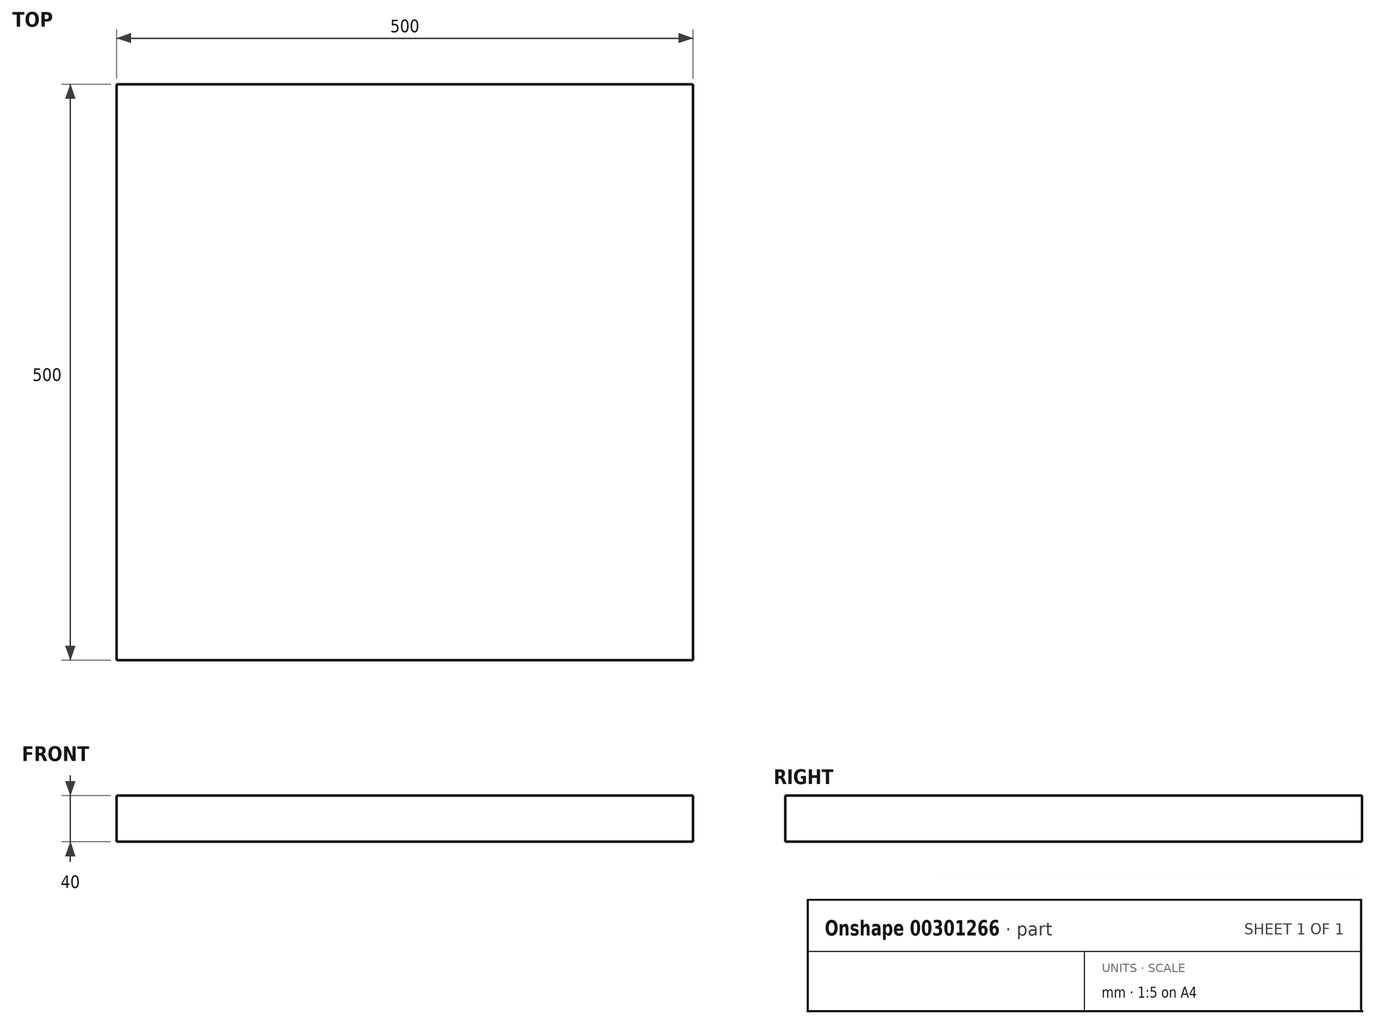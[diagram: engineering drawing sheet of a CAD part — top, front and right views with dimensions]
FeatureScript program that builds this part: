
annotation { "Feature Type Name" : "Feature", "Feature Type Description" : "" }
export const myFeature = defineFeature(function(context is Context, id is Id, definition is map)
    precondition{}
    {
        {
            var Q0;
            Q0=qCreatedBy(makeId("Top.planeOp"),FACE);
            var sketch = newSketch(context, id + "F0", { "sketchPlane" : qUnion([Q0])});
            skLineSegment(sketch, "E0.bottom", {"start": v(-250, 250) * mm, "end": v(250, 250) * mm});
            skLineSegment(sketch, "E0.top", {"start": v(-250, -250) * mm, "end": v(250, -250) * mm});
            skLineSegment(sketch, "E0.left", {"start": v(-250, 250) * mm, "end": v(-250, -250) * mm});
            skLineSegment(sketch, "E0.right", {"start": v(250, 250) * mm, "end": v(250, -250) * mm});
            skPoint(sketch, "E0.middle", {"position": v(0, 0) * mm});
            skSolve(sketch);
        }
        {
            var Q0;
            Q0 = qSketchRegion(id + "F0", true);
            extrude(context, id + "F1", {"entities" : qUnion([Q0]), "depth" : 40 * mm});
        }
    });
